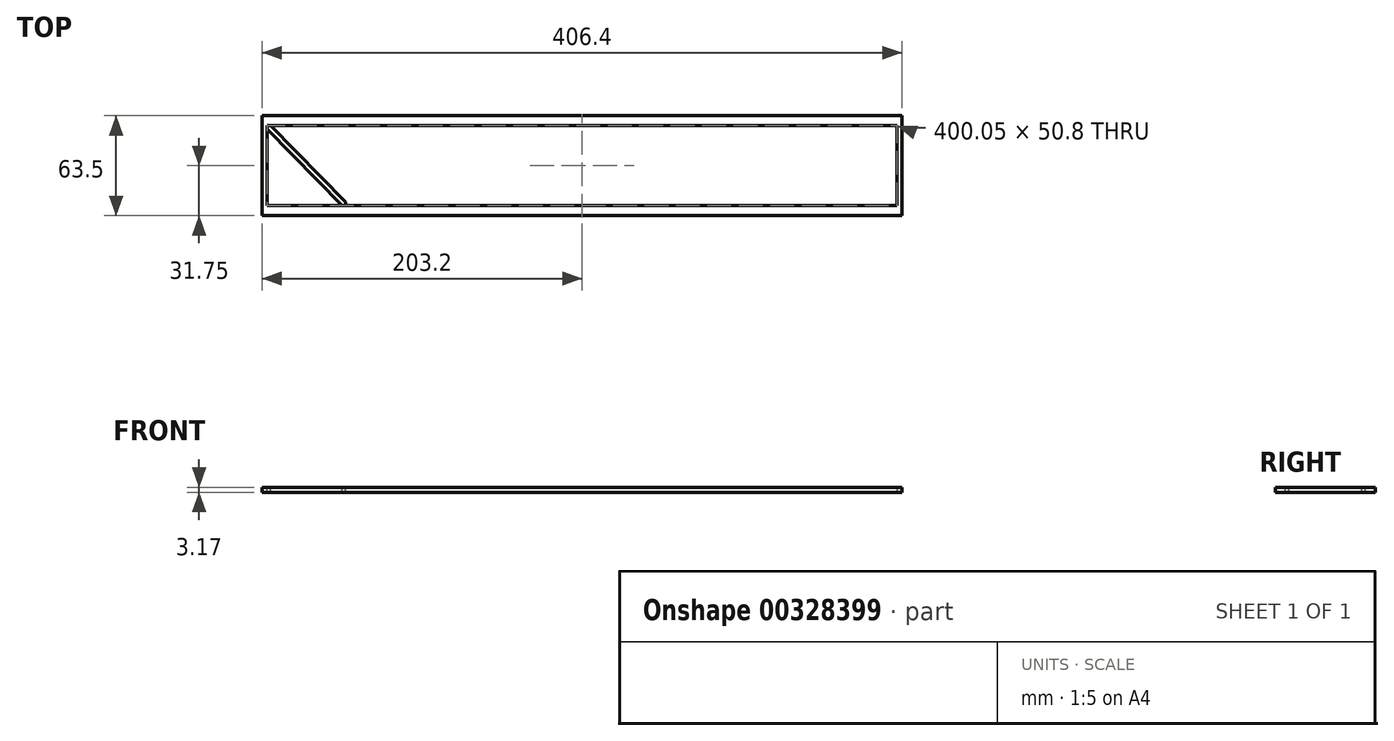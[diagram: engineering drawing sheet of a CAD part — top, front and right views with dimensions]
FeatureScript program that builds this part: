
annotation { "Feature Type Name" : "Feature", "Feature Type Description" : "" }
export const myFeature = defineFeature(function(context is Context, id is Id, definition is map)
    precondition{}
    {
        {
            var Q0;
            Q0=qCreatedBy(makeId("Top.planeOp"),FACE);
            var sketch = newSketch(context, id + "F0", { "sketchPlane" : qUnion([Q0])});
            skLineSegment(sketch, "E0.bottom", {"start": v(0, 0) * mm, "end": v(406.4, 0) * mm});
            skLineSegment(sketch, "E0.top", {"start": v(0, 63.5) * mm, "end": v(406.4, 63.5) * mm});
            skLineSegment(sketch, "E0.left", {"start": v(0, 0) * mm, "end": v(0, 63.5) * mm});
            skLineSegment(sketch, "E0.right", {"start": v(406.4, 0) * mm, "end": v(406.4, 63.5) * mm});
            skLineSegment(sketch, "E1.bottom", {"start": v(3.17, 6.35) * mm, "end": v(403.23, 6.35) * mm});
            skLineSegment(sketch, "E1.top", {"start": v(3.17, 57.15) * mm, "end": v(403.23, 57.15) * mm});
            skLineSegment(sketch, "E1.left", {"start": v(3.17, 6.35) * mm, "end": v(3.17, 57.15) * mm});
            skLineSegment(sketch, "E1.right", {"start": v(403.23, 6.35) * mm, "end": v(403.23, 57.15) * mm});
            skSolve(sketch);
        }
        {
            var Q0;
            Q0 = qSketchRegion(id + "F0", true);
            extrude(context, id + "F1", {"entities" : qUnion([Q0]), "depth" : 3.17 * mm});
        }
        {
            var Q0;
            Q0=makeQuery(id+"F1.opExtrude","CAP_FACE",FACE,{"disambiguationData":[OSD([sQuery(id+"F0.wireOp",EDGE,"E0.bottom"),sQuery(id+"F0.wireOp",EDGE,"E0.top"),sQuery(id+"F0.wireOp",EDGE,"E0.left"),sQuery(id+"F0.wireOp",EDGE,"E0.right"),sQuery(id+"F0.wireOp",EDGE,"E1.bottom"),sQuery(id+"F0.wireOp",EDGE,"E1.top"),sQuery(id+"F0.wireOp",EDGE,"E1.left"),sQuery(id+"F0.wireOp",EDGE,"E1.right")])],"isStart":false});
            var sketch = newSketch(context, id + "F2", { "sketchPlane" : qUnion([Q0])});
            skLineSegment(sketch, "E2", {"start": v(3.17, 57.15) * mm, "end": v(53.18, 6.35) * mm, "construction": true});
            skLineSegment(sketch, "E3", {"start": v(53.18, 6.35) * mm, "end": v(103.19, 57.15) * mm, "construction": true});
            skLineSegment(sketch, "E4", {"start": v(103.19, 57.15) * mm, "end": v(153.2, 6.35) * mm, "construction": true});
            skLineSegment(sketch, "E5", {"start": v(153.2, 6.35) * mm, "end": v(203.2, 57.15) * mm, "construction": true});
            skLineSegment(sketch, "E6", {"start": v(203.2, 57.15) * mm, "end": v(253.2, 6.35) * mm, "construction": true});
            skLineSegment(sketch, "E7", {"start": v(253.2, 6.35) * mm, "end": v(303.21, 57.15) * mm, "construction": true});
            skLineSegment(sketch, "E8", {"start": v(3.17, 57.15) * mm, "end": v(103.19, 57.15) * mm, "construction": true});
            skLineSegment(sketch, "E9", {"start": v(103.19, 57.15) * mm, "end": v(203.2, 57.15) * mm, "construction": true});
            skLineSegment(sketch, "E10", {"start": v(203.2, 57.15) * mm, "end": v(303.21, 57.15) * mm, "construction": true});
            skLineSegment(sketch, "E11", {"start": v(53.18, 6.35) * mm, "end": v(53.18, 57.15) * mm, "construction": true});
            skLineSegment(sketch, "E12", {"start": v(153.2, 6.35) * mm, "end": v(153.2, 57.15) * mm, "construction": true});
            skLineSegment(sketch, "E13", {"start": v(253.2, 6.35) * mm, "end": v(253.2, 57.15) * mm, "construction": true});
            skLineSegment(sketch, "E14", {"start": v(303.21, 57.15) * mm, "end": v(353.22, 6.35) * mm, "construction": true});
            skLineSegment(sketch, "E15", {"start": v(353.22, 6.35) * mm, "end": v(403.23, 57.15) * mm, "construction": true});
            skLineSegment(sketch, "E16", {"start": v(403.23, 57.15) * mm, "end": v(303.21, 57.15) * mm, "construction": true});
            skLineSegment(sketch, "E17", {"start": v(353.22, 6.35) * mm, "end": v(353.22, 57.15) * mm, "construction": true});
            skLineSegment(sketch, "E18.0", {"start": v(353.22, 4.09) * mm, "end": v(404.36, 56.04) * mm});
            skLineSegment(sketch, "E18.1", {"start": v(303.21, 54.89) * mm, "end": v(353.22, 4.09) * mm});
            skLineSegment(sketch, "E18.2", {"start": v(253.2, 4.09) * mm, "end": v(303.21, 54.89) * mm});
            skLineSegment(sketch, "E18.3", {"start": v(203.2, 54.89) * mm, "end": v(253.2, 4.09) * mm});
            skLineSegment(sketch, "E18.4", {"start": v(2.06, 56.02) * mm, "end": v(53.18, 4.09) * mm});
            skLineSegment(sketch, "E18.5", {"start": v(53.18, 4.09) * mm, "end": v(103.19, 54.89) * mm});
            skLineSegment(sketch, "E18.6", {"start": v(103.19, 54.89) * mm, "end": v(153.2, 4.09) * mm});
            skLineSegment(sketch, "E18.7", {"start": v(153.2, 4.09) * mm, "end": v(203.2, 54.89) * mm});
            skLineSegment(sketch, "E19.0", {"start": v(353.22, 8.61) * mm, "end": v(402.1, 58.26) * mm});
            skLineSegment(sketch, "E19.1", {"start": v(303.21, 59.41) * mm, "end": v(353.22, 8.61) * mm});
            skLineSegment(sketch, "E19.2", {"start": v(253.2, 8.61) * mm, "end": v(303.21, 59.41) * mm});
            skLineSegment(sketch, "E19.3", {"start": v(203.2, 59.41) * mm, "end": v(253.2, 8.61) * mm});
            skLineSegment(sketch, "E19.4", {"start": v(4.3, 58.26) * mm, "end": v(53.18, 8.61) * mm});
            skLineSegment(sketch, "E19.5", {"start": v(53.18, 8.61) * mm, "end": v(103.19, 59.41) * mm});
            skLineSegment(sketch, "E19.6", {"start": v(103.19, 59.41) * mm, "end": v(153.2, 8.61) * mm});
            skLineSegment(sketch, "E19.7", {"start": v(153.2, 8.61) * mm, "end": v(203.2, 59.41) * mm});
            skLineSegment(sketch, "E20", {"start": v(53.18, 6.35) * mm, "end": v(53.18, 8.61) * mm});
            skLineSegment(sketch, "E21", {"start": v(5.38, 54.91) * mm, "end": v(4.8, 55.5) * mm});
            skSolve(sketch);
        }
        {
            var Q0;
            {var subQ5=sQuery(id+"F2.wireOp",EDGE,"E20");Q0=makeQuery(id+"F2.imprint","IMPRINT",FACE,{"disambiguationData":[TD([[makeQuery(id+"F2.imprint","IMPRINT",EDGE,{"derivedFrom":subQ5}),1.0]])]});}
            extrude(context, id + "F3", {"entities" : qUnion([Q0]), "oppositeDirection" : true, "depth" : 3.17 * mm});
        }
    });
